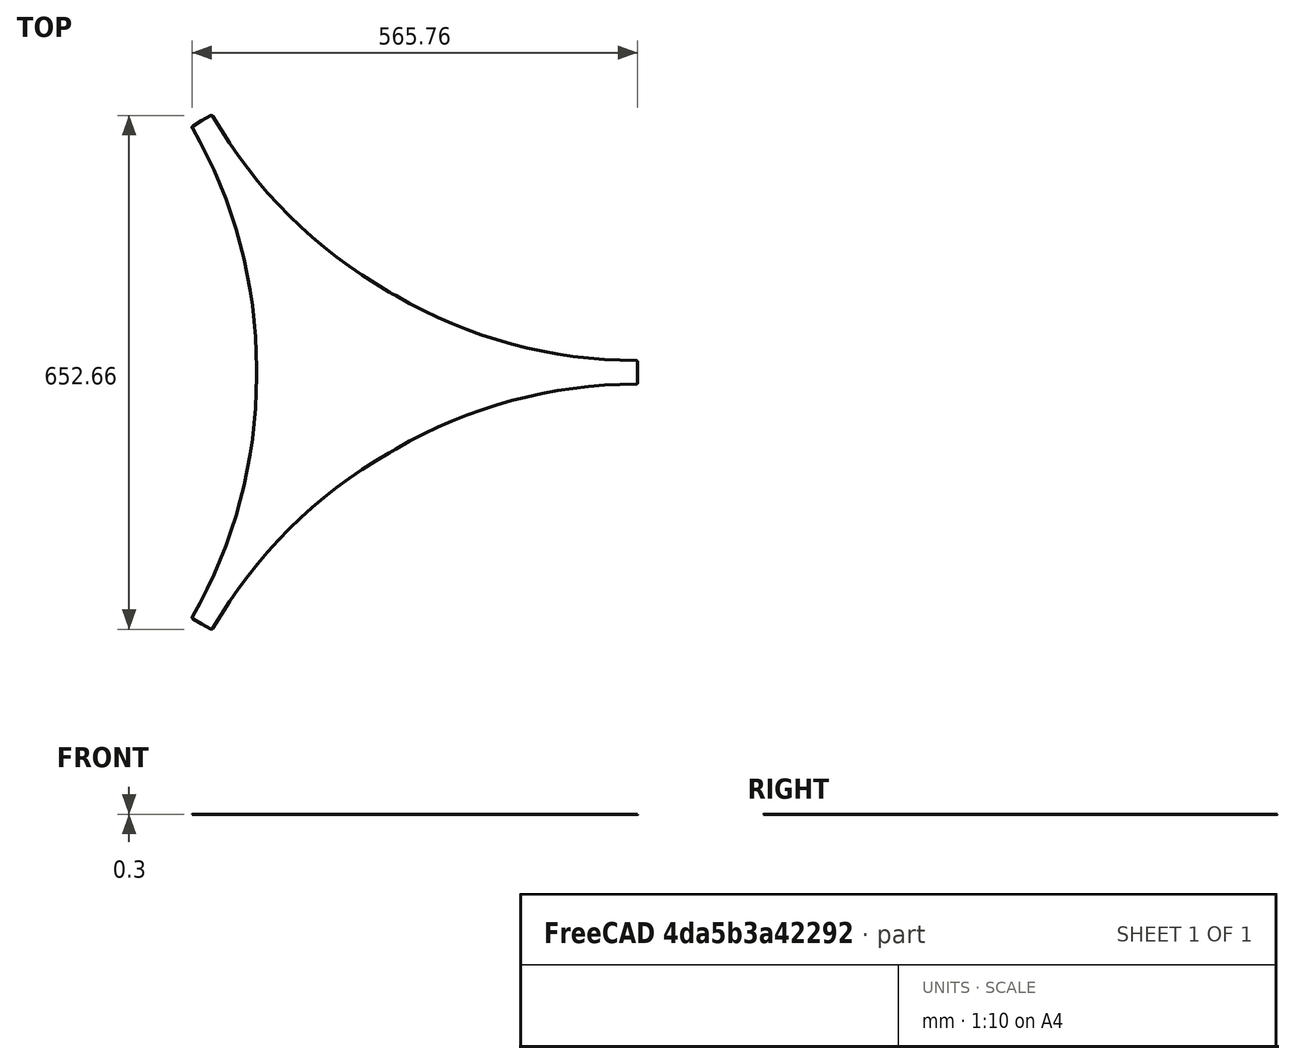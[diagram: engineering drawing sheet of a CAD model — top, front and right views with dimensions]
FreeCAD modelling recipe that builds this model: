
FCSTD DOCUMENT  (FreeCAD 1.1R38827 (Git))
Label: composit_stand3_hat_bottom_model
License: All rights reserved
LicenseURL: http://en.wikipedia.org/wiki/All_rights_reserved
objects: Part::FeaturePython×3, PartDesign::CoordinateSystem×2, PartDesign::SubShapeBinder×1, PartDesign::FeaturePython×1, PartDesign::Body×1, App::Link×1, Part::Mirroring×1, Part::Compound×1
note: 11 computed .brp shape members not serialized (recipe doc carries the construction recipe); baked Part::Feature solids carry a one-line shape summary decoded from their .brp
EXTERNAL_REF file=composit_stand3_hat_bottom_main.FCStd obj=Sketch

FEATURE [PartDesign::SubShapeBinder] Binder001
  BindCopyOnChange = 0
  BindMode = 0
  ClaimChildren = true
  Context = -> Body [Binder001.]
  Fuse = false
  MakeFace = true
  OffsetFill = false
  OffsetIntersection = false
  OffsetJoinType = 0
  OffsetOpenResult = false
  PartialLoad = false
  Relative = false
  Support = -> [Connect]
  _Version = 2
FEATURE [PartDesign::FeaturePython] BaseBend  # WARN: FeaturePython — macro-defined, semantics opaque (R4)
  BendSide = 0
  BendSketch = -> Binder001
  MidPlane = false
  Reverse = false
  Suppressed = false
  length = 100
  radius = 0.1
  thickness = 0.3
FEATURE [PartDesign::CoordinateSystem] Local_CS  label="botttom_LCS"
  AttacherType = Attacher::AttachEngine3D
  AttachmentSupport = -> [XY_Plane]
  MapMode = 5
FEATURE [PartDesign::CoordinateSystem] Local_CS001  label="top_LCS"
  AttacherType = Attacher::AttachEngine3D
  AttachmentOffset = pos=(0,0,3) rot=(0,0,1;0rad)
  AttachmentSupport = -> [XY_Plane]
  MapMode = 5
  Placement = pos=(0,0,3) rot=(0,0,1;0rad)
FEATURE [PartDesign::Body] Body  label="hat_bottom"
  AllowCompound = false
  Group = -> [Binder001,BaseBend,Local_CS,Local_CS001]
  Origin = -> Origin
  Tip = -> BaseBend
FEATURE [App::Link] Link  label="main_sketch"
  LinkedObject = -> <external composit_stand3_hat_bottom_main.FCStd>#Sketch
FEATURE [Part::Mirroring] Part__Mirroring  label="main_sketch (Mirror #1)"
  Base = (0,0,0)
  Normal = (0,1,0)
  Source = -> Link
FEATURE [Part::Compound] Compound
  Links = -> [Link,Part__Mirroring]
FEATURE [Part::FeaturePython] PolarArray  # WARN: FeaturePython — macro-defined, semantics opaque (R4)
  Alignment = 0
  AttacherType = Attacher::AttachEngine3D
  CellStart = A1
  Count = 3
  DistributionLaw = 0
  EndInclusive = false
  ExposePlacement = false
  FlipX = false
  FlipZ = false
  GeneratorMode = 0
  MarkerShape = 1
  MarkerSize = 50
  NumElements = 3
  OrientMode = 2
  Radius = 0
  Reverse = false
  SpanEnd = 360
  SpanStart = 0
  Step = 120
  Type = lattice2PolarArray2.PolarArray
  UseArcRadius = false
  UseArcRange = 0
  VSGVersion = 1
  Values = 0.0 | 120.0 | 240.0
  ValuesSource = 2
  isLattice = 1
FEATURE [Part::FeaturePython] Populate  label="Populate PolarArray with Compound"  # WARN: FeaturePython — macro-defined, semantics opaque (R4)
  Copying = 0
  ExposePlacement = false
  MarkerShape = 1
  MarkerSize = 0
  NumElements = 0
  Object = -> Compound
  OutputCompounding = 1
  PlacementsTo = -> PolarArray
  Referencing = 0
  Type = lattice2PopulateCopies.LatticePopulateCopies
  isLattice = 0
FEATURE [Part::FeaturePython] Connect  # WARN: FeaturePython — macro-defined, semantics opaque (R4)
  Objects = -> [Populate]
  Tolerance = 0
